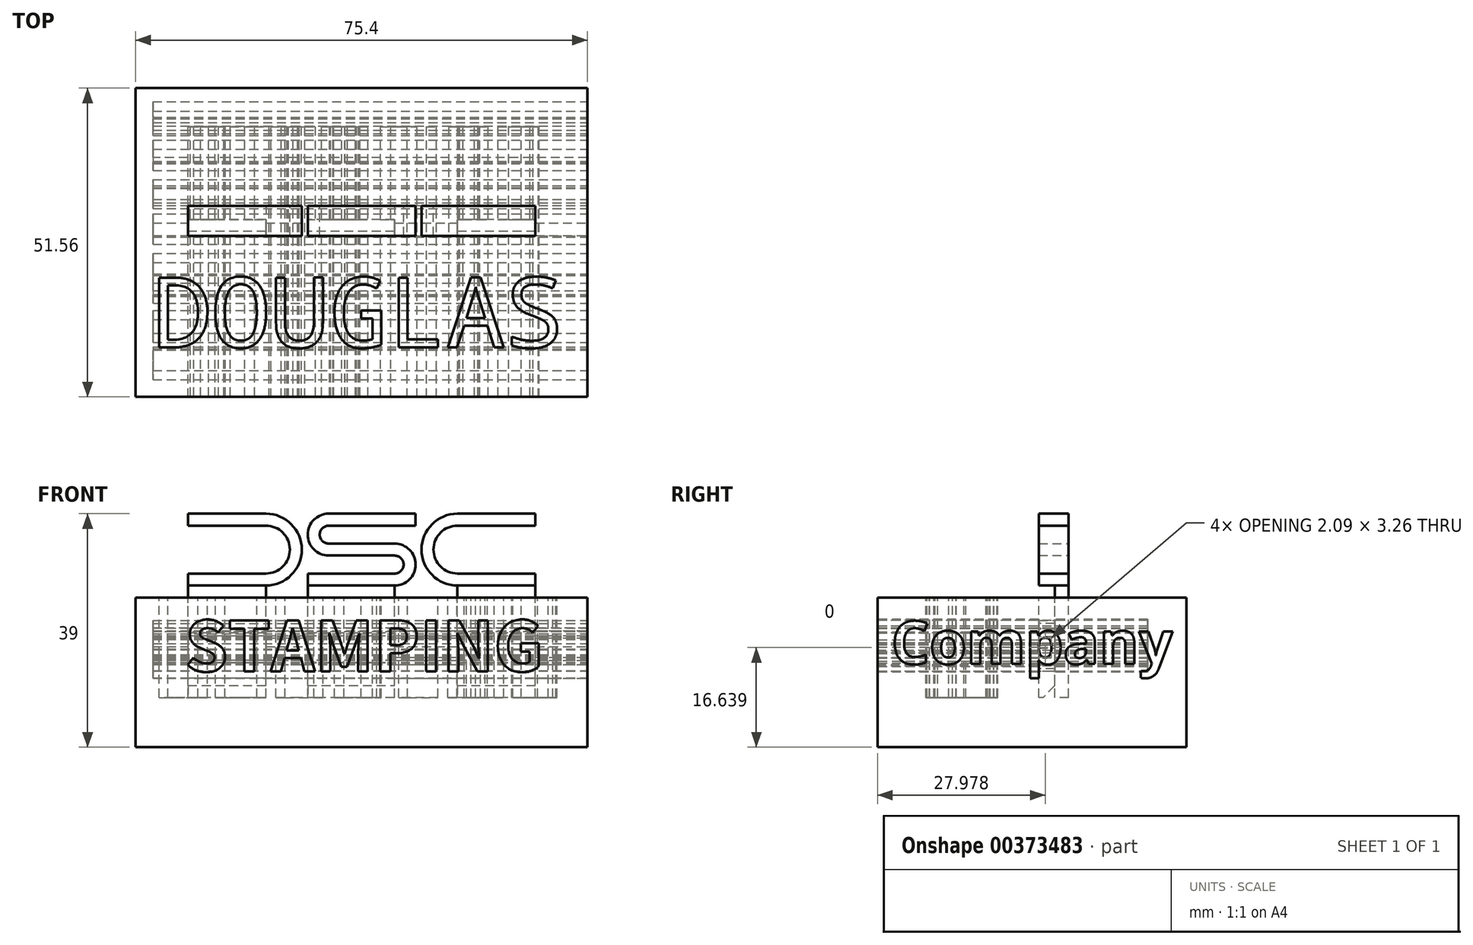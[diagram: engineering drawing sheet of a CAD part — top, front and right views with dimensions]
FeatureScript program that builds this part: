
annotation { "Feature Type Name" : "Feature", "Feature Type Description" : "" }
export const myFeature = defineFeature(function(context is Context, id is Id, definition is map)
    precondition{}
    {
        {
            var Q0;
            Q0=qCreatedBy(makeId("Front.planeOp"),FACE);
            var sketch = newSketch(context, id + "F0", { "sketchPlane" : qUnion([Q0])});
            skLineSegment(sketch, "E0.bottom", {"start": v(24, 6) * mm, "end": v(11, 6) * mm});
            skLineSegment(sketch, "E0.top", {"start": v(24, -6) * mm, "end": v(11, -6) * mm});
            skLineSegment(sketch, "E0.left", {"start": v(30, 0) * mm, "end": v(30, 0) * mm});
            skLineSegment(sketch, "E0.right", {"start": v(-30, 0) * mm, "end": v(-30, 0) * mm});
            skPoint(sketch, "E0.middle", {"position": v(0, 0) * mm});
            skPoint(sketch, "E1.visualSharp", {"position": v(-30, 6) * mm});
            skArc(sketch, "E1.filletArc", {"start": v(-24, 6) * mm, "mid": v(-28.24, 4.24) * mm, "end": v(-30, 0) * mm});
            skPoint(sketch, "E2.visualSharp", {"position": v(-30, -6) * mm});
            skArc(sketch, "E2.filletArc", {"start": v(-30, 0) * mm, "mid": v(-28.24, -4.24) * mm, "end": v(-24, -6) * mm});
            skPoint(sketch, "E3.visualSharp", {"position": v(30, 6) * mm});
            skArc(sketch, "E3.filletArc", {"start": v(30, 0) * mm, "mid": v(28.24, 4.24) * mm, "end": v(24, 6) * mm});
            skPoint(sketch, "E4.visualSharp", {"position": v(30, -6) * mm});
            skArc(sketch, "E4.filletArc", {"start": v(24, -6) * mm, "mid": v(28.24, -4.24) * mm, "end": v(30, 0) * mm});
            skArc(sketch, "E5.0", {"start": v(-24, 4) * mm, "mid": v(-26.83, 2.83) * mm, "end": v(-28, 0) * mm});
            skArc(sketch, "E6.MirrorCS", {"start": v(-24, -4) * mm, "mid": v(-26.83, -2.83) * mm, "end": v(-28, 0) * mm});
            skArc(sketch, "E7.MirrorCS", {"start": v(24, 4) * mm, "mid": v(26.83, 2.83) * mm, "end": v(28, 0) * mm});
            skArc(sketch, "E8.MirrorCS", {"start": v(24, -4) * mm, "mid": v(26.83, -2.83) * mm, "end": v(28, 0) * mm});
            skLineSegment(sketch, "E9", {"start": v(-24, 4) * mm, "end": v(-11, 4) * mm});
            skLineSegment(sketch, "E10", {"start": v(-24, -4) * mm, "end": v(-11, -4) * mm});
            skLineSegment(sketch, "E11", {"start": v(-11, 6) * mm, "end": v(-11, 4) * mm});
            skLineSegment(sketch, "E12.MirrorCS", {"start": v(11, 6) * mm, "end": v(11, 4) * mm});
            skLineSegment(sketch, "E13.trimOffspring", {"start": v(-11, 6) * mm, "end": v(-24, 6) * mm});
            skLineSegment(sketch, "E14.trimOffspring", {"start": v(-5.5, 4) * mm, "end": v(9, 4) * mm});
            skLineSegment(sketch, "E15.trimOffspring", {"start": v(-11, -4) * mm, "end": v(-11, -6) * mm});
            skLineSegment(sketch, "E16.trimOffspring", {"start": v(-9, -4) * mm, "end": v(5.5, -4) * mm});
            skLineSegment(sketch, "E17.trimOffspring", {"start": v(-11, -6) * mm, "end": v(-24, -6) * mm});
            skLineSegment(sketch, "E18.trimOffspring", {"start": v(9, 6) * mm, "end": v(-5.5, 6) * mm});
            skLineSegment(sketch, "E19.trimOffspring", {"start": v(11, 4) * mm, "end": v(24, 4) * mm});
            skLineSegment(sketch, "E20.trimOffspring", {"start": v(11, -4) * mm, "end": v(24, -4) * mm});
            skLineSegment(sketch, "E21.trimOffspring", {"start": v(5.5, -6) * mm, "end": v(-9, -6) * mm});
            skLineSegment(sketch, "E22.trimOffspring", {"start": v(11, -4) * mm, "end": v(11, -6) * mm});
            skLineSegment(sketch, "E23.MirrorCS", {"start": v(-5.5, -1) * mm, "end": v(5.5, -1) * mm});
            skLineSegment(sketch, "E24", {"start": v(-9, 2.5) * mm, "end": v(9, 2.5) * mm, "construction": true});
            skLineSegment(sketch, "E25", {"start": v(-9, -2.5) * mm, "end": v(9, -2.5) * mm, "construction": true});
            skArc(sketch, "E26", {"start": v(-5.5, 6) * mm, "mid": v(-9, 2.5) * mm, "end": v(-5.5, -1) * mm});
            skArc(sketch, "E27", {"start": v(-5.5, 4) * mm, "mid": v(-7, 2.5) * mm, "end": v(-5.5, 1) * mm});
            skArc(sketch, "E28", {"start": v(5.5, -6) * mm, "mid": v(9, -2.5) * mm, "end": v(5.5, 1) * mm});
            skArc(sketch, "E29", {"start": v(5.5, -4) * mm, "mid": v(7, -2.5) * mm, "end": v(5.5, -1) * mm});
            skPoint(sketch, "E30.orphan", {"position": v(-9, 6) * mm});
            skPoint(sketch, "E31.orphan", {"position": v(-9, 4) * mm});
            skLineSegment(sketch, "E32.trimOffspring", {"start": v(-5.5, 1) * mm, "end": v(5.5, 1) * mm});
            skPoint(sketch, "E33.start.orphan", {"position": v(-9, 1) * mm});
            skLineSegment(sketch, "E34", {"start": v(9, 6) * mm, "end": v(9, 4) * mm});
            skLineSegment(sketch, "E35", {"start": v(-9, -4) * mm, "end": v(-9, -6) * mm});
            skPoint(sketch, "E36.orphan", {"position": v(-9, -1) * mm});
            skPoint(sketch, "E37.start.orphan", {"position": v(9, 1) * mm});
            skPoint(sketch, "E38.orphan", {"position": v(9, -6) * mm});
            skPoint(sketch, "E39.orphan", {"position": v(9, -1) * mm});
            skPoint(sketch, "E40.orphan", {"position": v(9, -4) * mm});
            skSolve(sketch);
        }
        {
            var Q0;
            Q0=makeQuery(id+"F0.imprint","IMPRINT",FACE,{"disambiguationData":[TD([[makeQuery(id+"F0.imprint","IMPRINT",EDGE,{"derivedFrom":sQuery(id+"F0.wireOp",EDGE,"E1.filletArc")}),1.0]])]});
            var Q1;
            Q1=makeQuery(id+"F0.imprint","IMPRINT",FACE,{"disambiguationData":[TD([[makeQuery(id+"F0.imprint","IMPRINT",EDGE,{"derivedFrom":sQuery(id+"F0.wireOp",EDGE,"E14.trimOffspring")}),1.0]])]});
            var Q2;
            Q2=makeQuery(id+"F0.imprint","IMPRINT",FACE,{"disambiguationData":[TD([[makeQuery(id+"F0.imprint","IMPRINT",EDGE,{"derivedFrom":sQuery(id+"F0.wireOp",EDGE,"E0.bottom")}),1.0]])]});
            extrude(context, id + "F1", {"entities" : qUnion([Q0, Q1, Q2]), "depth" : 5 * mm});
        }
        {
            var Q0;
            Q0=makeQuery(id+"F1.opExtrude","SWEPT_BODY",BODY,{"disambiguationData":[OSD([sQuery(id+"F0.wireOp",EDGE,"E1.filletArc"),sQuery(id+"F0.wireOp",EDGE,"E2.filletArc"),sQuery(id+"F0.wireOp",EDGE,"E6.MirrorCS"),sQuery(id+"F0.wireOp",EDGE,"E5.0"),sQuery(id+"F0.wireOp",EDGE,"E9"),sQuery(id+"F0.wireOp",EDGE,"E10"),sQuery(id+"F0.wireOp",EDGE,"E11"),sQuery(id+"F0.wireOp",EDGE,"E13.trimOffspring"),sQuery(id+"F0.wireOp",EDGE,"E15.trimOffspring"),sQuery(id+"F0.wireOp",EDGE,"E17.trimOffspring")])]});
            var Q1;
            Q1=makeQuery(id+"F1.opExtrude","CAP_EDGE",EDGE,{"disambiguationData":[OSD([sQuery(id+"F0.wireOp",EDGE,"E10")])],"isStart":false});
            transform(context, id + "F2", {"entities" : qUnion([Q0]), "transformType" : TransformType.TRANSLATION_DISTANCE, "transformDirection" : qUnion([Q1]), "distance" : 40 * mm, "makeCopy" : false});
        }
        {
            var Q0;
            Q0=makeQuery(id+"F1.opExtrude","SWEPT_BODY",BODY,{"disambiguationData":[OSD([sQuery(id+"F0.wireOp",EDGE,"E0.bottom"),sQuery(id+"F0.wireOp",EDGE,"E0.top"),sQuery(id+"F0.wireOp",EDGE,"E3.filletArc"),sQuery(id+"F0.wireOp",EDGE,"E4.filletArc"),sQuery(id+"F0.wireOp",EDGE,"E7.MirrorCS"),sQuery(id+"F0.wireOp",EDGE,"E8.MirrorCS"),sQuery(id+"F0.wireOp",EDGE,"E12.MirrorCS"),sQuery(id+"F0.wireOp",EDGE,"E19.trimOffspring"),sQuery(id+"F0.wireOp",EDGE,"E20.trimOffspring"),sQuery(id+"F0.wireOp",EDGE,"E22.trimOffspring")])]});
            var Q1;
            Q1=makeQuery(id+"F1.opExtrude","CAP_EDGE",EDGE,{"disambiguationData":[OSD([sQuery(id+"F0.wireOp",EDGE,"E16.trimOffspring")])],"isStart":false});
            transform(context, id + "F3", {"entities" : qUnion([Q0]), "transformType" : TransformType.TRANSLATION_DISTANCE, "transformDirection" : qUnion([Q1]), "distance" : 40 * mm, "oppositeDirection" : true, "makeCopy" : false});
        }
        {
            var Q0;
            Q0=makeQuery(id+"F1.opExtrude","SWEPT_BODY",BODY,{"disambiguationData":[OSD([sQuery(id+"F0.wireOp",EDGE,"E0.bottom"),sQuery(id+"F0.wireOp",EDGE,"E0.top"),sQuery(id+"F0.wireOp",EDGE,"E3.filletArc"),sQuery(id+"F0.wireOp",EDGE,"E4.filletArc"),sQuery(id+"F0.wireOp",EDGE,"E7.MirrorCS"),sQuery(id+"F0.wireOp",EDGE,"E8.MirrorCS"),sQuery(id+"F0.wireOp",EDGE,"E12.MirrorCS"),sQuery(id+"F0.wireOp",EDGE,"E19.trimOffspring"),sQuery(id+"F0.wireOp",EDGE,"E20.trimOffspring"),sQuery(id+"F0.wireOp",EDGE,"E22.trimOffspring")])]});
            var Q1;
            Q1=makeQuery(id+"F1.opExtrude","SWEPT_BODY",BODY,{"disambiguationData":[OSD([sQuery(id+"F0.wireOp",EDGE,"E1.filletArc"),sQuery(id+"F0.wireOp",EDGE,"E2.filletArc"),sQuery(id+"F0.wireOp",EDGE,"E6.MirrorCS"),sQuery(id+"F0.wireOp",EDGE,"E5.0"),sQuery(id+"F0.wireOp",EDGE,"E9"),sQuery(id+"F0.wireOp",EDGE,"E10"),sQuery(id+"F0.wireOp",EDGE,"E11"),sQuery(id+"F0.wireOp",EDGE,"E13.trimOffspring"),sQuery(id+"F0.wireOp",EDGE,"E15.trimOffspring"),sQuery(id+"F0.wireOp",EDGE,"E17.trimOffspring")])]});
            var Q2;
            Q2=makeQuery(id+"F1.opExtrude","SWEPT_BODY",BODY,{"disambiguationData":[OSD([sQuery(id+"F0.wireOp",EDGE,"E14.trimOffspring"),sQuery(id+"F0.wireOp",EDGE,"E16.trimOffspring"),sQuery(id+"F0.wireOp",EDGE,"E18.trimOffspring"),sQuery(id+"F0.wireOp",EDGE,"E21.trimOffspring"),sQuery(id+"F0.wireOp",EDGE,"E23.MirrorCS"),sQuery(id+"F0.wireOp",EDGE,"E26"),sQuery(id+"F0.wireOp",EDGE,"E27"),sQuery(id+"F0.wireOp",EDGE,"E28"),sQuery(id+"F0.wireOp",EDGE,"E29"),sQuery(id+"F0.wireOp",EDGE,"E32.trimOffspring"),sQuery(id+"F0.wireOp",EDGE,"E34"),sQuery(id+"F0.wireOp",EDGE,"E35")])]});
            transform(context, id + "F4", {"entities" : qUnion([Q0, Q1, Q2]), "transformType" : TransformType.TRANSLATION_3D, "dx" : 0 * mm, "dy" : 0 * mm, "dz" : 8 * mm, "makeCopy" : false});
        }
        {
            var Q0;
            Q0=qCreatedBy(makeId("Top.planeOp"),FACE);
            var sketch = newSketch(context, id + "F5", { "sketchPlane" : qUnion([Q0])});
            skLineSegment(sketch, "E41.bottom", {"start": v(-37.74, 19.66) * mm, "end": v(37.66, 19.66) * mm});
            skLineSegment(sketch, "E41.top", {"start": v(-37.74, -31.9) * mm, "end": v(37.66, -31.9) * mm});
            skLineSegment(sketch, "E41.left", {"start": v(-37.74, 19.66) * mm, "end": v(-37.74, -31.9) * mm});
            skLineSegment(sketch, "E41.right", {"start": v(37.66, 19.66) * mm, "end": v(37.66, -31.9) * mm});
            skSolve(sketch);
        }
        {
            var Q0;
            Q0=makeQuery(id+"F5.imprint","IMPRINT",FACE,{"disambiguationData":[TD([[makeQuery(id+"F5.imprint","IMPRINT",EDGE,{"derivedFrom":sQuery(id+"F5.wireOp",EDGE,"E41.bottom")}),-1.0]])]});
            extrude(context, id + "F6", {"entities" : qUnion([Q0]), "oppositeDirection" : true, "depth" : 25 * mm});
        }
        {
            var Q0;
            Q0=makeQuery(id+"F6.opExtrude","CAP_FACE",FACE,{"disambiguationData":[OSD([sQuery(id+"F5.wireOp",EDGE,"E41.bottom"),sQuery(id+"F5.wireOp",EDGE,"E41.top"),sQuery(id+"F5.wireOp",EDGE,"E41.left"),sQuery(id+"F5.wireOp",EDGE,"E41.right")])],"isStart":true});
            var sketch = newSketch(context, id + "F7", { "sketchPlane" : qUnion([Q0])});
            skText(sketch, "E42", { "text": "DOUGLAS", "fontName": "DroidSansMono.ttf"});
            const initialGuessF7  = {"E42": [-0.03491, -0.02366, 1, 0, 0.01177]};
            skSetInitialGuess(sketch, initialGuessF7);
            skSolve(sketch);
        }
        {
            var Q0;
            Q0=qSketchRegion(id+"F7",true);
            extrude(context, id + "F8", {"entities" : qUnion([Q0]), "oppositeDirection" : true, "depth" : 16.7 * mm});
        }
        {
            var Q0;
            Q0=makeQuery(id+"F6.opExtrude","SWEPT_FACE",FACE,{"disambiguationData":[OSD([sQuery(id+"F5.wireOp",EDGE,"E41.top")])]});
            var sketch = newSketch(context, id + "F9", { "sketchPlane" : qUnion([Q0])});
            skText(sketch, "E43", { "text": "STAMPING", "fontName": "NotoSansCJKsc-Bold.otf"});
            const initialGuessF9  = {"E43": [-0.02953, -0.01233, 1, 0, 0.00828]};
            skSetInitialGuess(sketch, initialGuessF9);
            skSolve(sketch);
        }
        {
            var Q0;
            Q0=qSketchRegion(id+"F9",true);
            extrude(context, id + "F10", {"entities" : qUnion([Q0]), "oppositeDirection" : true, "depth" : 45.1 * mm});
        }
        {
            var Q0;
            Q0=makeQuery(id+"F6.opExtrude","SWEPT_FACE",FACE,{"disambiguationData":[OSD([sQuery(id+"F5.wireOp",EDGE,"E41.right")])]});
            var sketch = newSketch(context, id + "F11", { "sketchPlane" : qUnion([Q0])});
            skText(sketch, "E44", { "text": "Company", "fontName": "OpenSans-Bold.ttf"});
            const initialGuessF11  = {"E44": [-0.02962, -0.0111, 1, 0, 0.0072]};
            skSetInitialGuess(sketch, initialGuessF11);
            skSolve(sketch);
        }
        {
            var Q0;
            Q0 = qSketchRegion(id + "F11", true);
            extrude(context, id + "F12", {"entities" : qUnion([Q0]), "oppositeDirection" : true, "depth" : 72.5 * mm});
        }
        {
            var Q0;
            Q0=makeQuery(id+"F1.opExtrude","SWEPT_FACE",FACE,{"disambiguationData":[OSD([sQuery(id+"F0.wireOp",EDGE,"E17.trimOffspring")])]});
            var Q1;
            Q1=makeQuery(id+"F1.opExtrude","SWEPT_FACE",FACE,{"disambiguationData":[OSD([sQuery(id+"F0.wireOp",EDGE,"E21.trimOffspring")])]});
            var Q2;
            Q2=makeQuery(id+"F1.opExtrude","SWEPT_FACE",FACE,{"disambiguationData":[OSD([sQuery(id+"F0.wireOp",EDGE,"E0.top")])]});
            var Q3;
            Q3=makeQuery(id+"F8.opExtrude","CAP_FACE",FACE,{"disambiguationData":[OSD([sQuery(id+"F7.wireOp",EDGE,"E42.sketch_text.stroke-35"),sQuery(id+"F7.wireOp",EDGE,"E42.sketch_text.stroke-36"),sQuery(id+"F7.wireOp",EDGE,"E42.sketch_text.stroke-37"),sQuery(id+"F7.wireOp",EDGE,"E42.sketch_text.stroke-38"),sQuery(id+"F7.wireOp",EDGE,"E42.sketch_text.stroke-39"),sQuery(id+"F7.wireOp",EDGE,"E42.sketch_text.stroke-40"),sQuery(id+"F7.wireOp",EDGE,"E42.sketch_text.stroke-41"),sQuery(id+"F7.wireOp",EDGE,"E42.sketch_text.stroke-42"),sQuery(id+"F7.wireOp",EDGE,"E42.sketch_text.stroke-43"),sQuery(id+"F7.wireOp",EDGE,"E42.sketch_text.stroke-44"),sQuery(id+"F7.wireOp",EDGE,"E42.sketch_text.stroke-45"),sQuery(id+"F7.wireOp",EDGE,"E42.sketch_text.stroke-46"),sQuery(id+"F7.wireOp",EDGE,"E42.sketch_text.stroke-47"),sQuery(id+"F7.wireOp",EDGE,"E42.sketch_text.stroke-48"),sQuery(id+"F7.wireOp",EDGE,"E42.sketch_text.stroke-49"),sQuery(id+"F7.wireOp",EDGE,"E42.sketch_text.stroke-50"),sQuery(id+"F7.wireOp",EDGE,"E42.sketch_text.stroke-51")])],"isStart":false});
            extrude(context, id + "F13", {"entities" : qUnion([Q0, Q1, Q2]), "endBound" : BoundingType.UP_TO_SURFACE, "endBoundEntityFace" : qUnion([Q3]), "depth" : 25 * mm});
        }
        {
            var Q0;
            {var subQ0=sQuery(id+"F0.wireOp",EDGE,"E0.top");Q0=makeQuery(id+"F13.opExtrude","SWEPT_FACE",FACE,{"disambiguationData":[OSD([subQ0]),TDD([makeQuery(id+"F1.opExtrude","CAP_EDGE",EDGE,{"disambiguationData":[OSD([subQ0])],"isStart":false})])]});}
            var Q1;
            {var subQ0=sQuery(id+"F0.wireOp",EDGE,"E21.trimOffspring");Q1=makeQuery(id+"F13.opExtrude","SWEPT_FACE",FACE,{"disambiguationData":[OSD([subQ0]),TDD([makeQuery(id+"F1.opExtrude","CAP_EDGE",EDGE,{"disambiguationData":[OSD([subQ0])],"isStart":false})])]});}
            var Q2;
            {var subQ0=sQuery(id+"F0.wireOp",EDGE,"E17.trimOffspring");Q2=makeQuery(id+"F13.opExtrude","SWEPT_FACE",FACE,{"disambiguationData":[OSD([subQ0]),TDD([makeQuery(id+"F1.opExtrude","CAP_EDGE",EDGE,{"disambiguationData":[OSD([subQ0])],"isStart":false})])]});}
            extrude(context, id + "F14", {"entities" : qUnion([Q0, Q1, Q2]), "operationType" : NewBodyOperationType.REMOVE, "oppositeDirection" : true, "depth" : 2.7 * mm});
        }
        {
            var Q0;
            Q0=makeQuery(id+"F14.boolean.opBoolean","COPY",EDGE,{"derivedFrom":makeQuery(id+"F14.opExtrude","CAP_EDGE",EDGE,{"disambiguationData":[OSD([sQuery(id+"F0.wireOp",EDGE,"E17.trimOffspring")])],"isStart":false})});
            var Q1;
            Q1=makeQuery(id+"F14.boolean.opBoolean","COPY",EDGE,{"derivedFrom":makeQuery(id+"F14.opExtrude","CAP_EDGE",EDGE,{"disambiguationData":[OSD([sQuery(id+"F0.wireOp",EDGE,"E21.trimOffspring")])],"isStart":false})});
            var Q2;
            Q2=makeQuery(id+"F14.boolean.opBoolean","COPY",EDGE,{"derivedFrom":makeQuery(id+"F14.opExtrude","CAP_EDGE",EDGE,{"disambiguationData":[OSD([sQuery(id+"F0.wireOp",EDGE,"E0.top")])],"isStart":false})});
            chamfer(context, id + "F15", {"entities" : qUnion([Q0, Q1, Q2]), "width" : 2 * mm, "tangentPropagation" : true});
        }
    });
